SOLIDWORKS PART (.sldprt)
format: sldprt  version: not decoded by parser v0  size: 276,480 bytes
history: native  units: mm
features: sketch x7, plane x6, extrude x4, mirror x2, material x1, sweep x1, revolve x1 (+10 scaffold rows collapsed)
feature tree (32):
  scaffold x10  (default folders/planes/origin — collapsed)
  material  "Matériau <non spécifié>"
  plane  "Plan de face"
  plane  "Plan de dessus"
  plane  "Plan de droite"
  sketch  "Esquisse1"  dims[D1=12.0mm]
  extrude  "Extrusion2"  Depth=3.5mm
  sketch  "Esquisse2"  dims[D1=10.0mm]
  extrude  "Extrusion5"  Depth=0.01mm
  sketch  "Esquisse6"  dims[D1=~0.44248mm]
  extrude  "Extrusion6"  Depth=0.5mm
  sketch  "Esquisse7"  dims[D1=~2.385657mm]
  extrude  "Extrusion7"  Depth=0.8mm
  plane  "Plan2"  Offset=0.05mm
  sketch  "Esquisse10"  dims[D1=2.5mm D2=1.0mm D3=0.2mm D4=0.5mm D5=1.0mm D6=0.1mm]
  sketch  "Esquisse3D4"  dims[c1.D1=1.0mm c1.D2=1.0mm c1.D3=0.2mm c2.D1=1.0mm c2.D2=1.0mm c3.D1=~6.904333mm c3.D2=3.5mm]
  sweep  "Balayage2"
  sketch  "Esquisse11"  dims[D7=1.0mm D8=0.2mm D1=1.3mm D2=5.75mm D3=5.7mm D4=1.2mm D5=0.6mm D6=2.7mm]
  revolve  "Révolution2"  Angle=360deg
  plane  "Plan3"  Offset=6mm
  plane  "Plan4"  Offset=6mm
  mirror  "Symétrie2"
  mirror  "Symétrie3"
decode coverage: 12 of 15 modeling features carry decoded parameters
note: ~ marks probable driven/reference dimensions
note: suppression state not decoded; provenance and decode notes live in map.json
